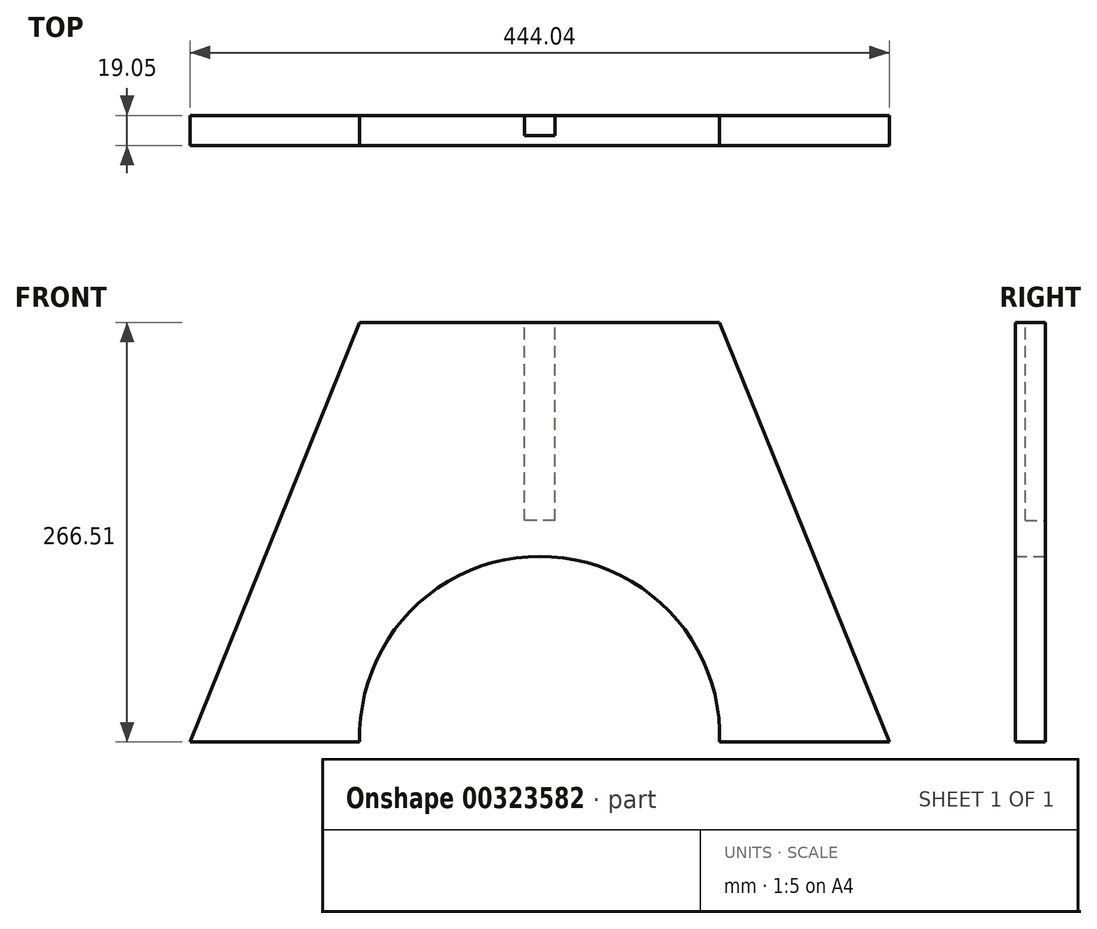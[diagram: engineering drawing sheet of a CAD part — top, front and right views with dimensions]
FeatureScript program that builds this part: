
annotation { "Feature Type Name" : "Feature", "Feature Type Description" : "" }
export const myFeature = defineFeature(function(context is Context, id is Id, definition is map)
    precondition{}
    {
        {
            var Q0;
            Q0=qCreatedBy(makeId("Front.planeOp"),FACE);
            var sketch = newSketch(context, id + "F0", { "sketchPlane" : qUnion([Q0])});
            skLineSegment(sketch, "E0", {"start": v(0, 149.93) * mm, "end": v(114.3, 149.93) * mm});
            skLineSegment(sketch, "E1", {"start": v(0, 149.93) * mm, "end": v(-114.3, 149.93) * mm});
            skLineSegment(sketch, "E2", {"start": v(114.3, 149.93) * mm, "end": v(222.02, -116.58) * mm});
            skLineSegment(sketch, "E3", {"start": v(222.02, -116.58) * mm, "end": v(114.3, -116.58) * mm});
            skLineSegment(sketch, "E4", {"start": v(0, 149.93) * mm, "end": v(0, 1.4) * mm, "construction": true});
            skLineSegment(sketch, "E5.MirrorCS", {"start": v(-114.3, 149.93) * mm, "end": v(-222.02, -116.58) * mm});
            skLineSegment(sketch, "E6.MirrorCS", {"start": v(-222.02, -116.58) * mm, "end": v(-114.3, -116.58) * mm});
            skArc(sketch, "E7", {"start": v(114.3, -116.58) * mm, "mid": v(0, 1.4) * mm, "end": v(-114.3, -116.58) * mm});
            skPoint(sketch, "E7.third.point", {"position": v(-114.3, -109.32) * mm});
            skLineSegment(sketch, "E8.trimOffspring", {"start": v(0, -112.95) * mm, "end": v(0, -115.14) * mm, "construction": true});
            skSolve(sketch);
        }
        {
            var Q0;
            Q0=qSketchRegion(id+"F0",true);
            extrude(context, id + "F1", {"entities" : qUnion([Q0]), "depth" : 19.05 * mm});
        }
        {
            var Q0;
            Q0=qCreatedBy(makeId("Front.planeOp"),FACE);
            var sketch = newSketch(context, id + "F2", { "sketchPlane" : qUnion([Q0])});
            skLineSegment(sketch, "E9", {"start": v(0, 0) * mm, "end": v(0, 24.15) * mm, "construction": true});
            skLineSegment(sketch, "E10", {"start": v(0, 24.15) * mm, "end": v(-9.65, 24.15) * mm});
            skPoint(sketch, "E11.orphan", {"position": v(0, 96.49) * mm});
            skLineSegment(sketch, "E12", {"start": v(0, 24.15) * mm, "end": v(0, 157.41) * mm, "construction": true});
            skLineSegment(sketch, "E13.MirrorCS", {"start": v(0, 24.15) * mm, "end": v(9.65, 24.15) * mm});
            skLineSegment(sketch, "E14", {"start": v(9.65, 24.15) * mm, "end": v(9.65, 151.1) * mm});
            skLineSegment(sketch, "E15", {"start": v(9.65, 151.1) * mm, "end": v(0, 151.1) * mm});
            skLineSegment(sketch, "E16.MirrorCS", {"start": v(-9.65, 24.15) * mm, "end": v(-9.65, 151.1) * mm});
            skLineSegment(sketch, "E17.MirrorCS", {"start": v(-9.65, 151.1) * mm, "end": v(0, 151.1) * mm});
            skSolve(sketch);
        }
        {
            var Q0;
            Q0 = qSketchRegion(id + "F2", true);
            extrude(context, id + "F3", {"entities" : qUnion([Q0]), "operationType" : NewBodyOperationType.REMOVE, "depth" : 12.7 * mm});
        }
    });
